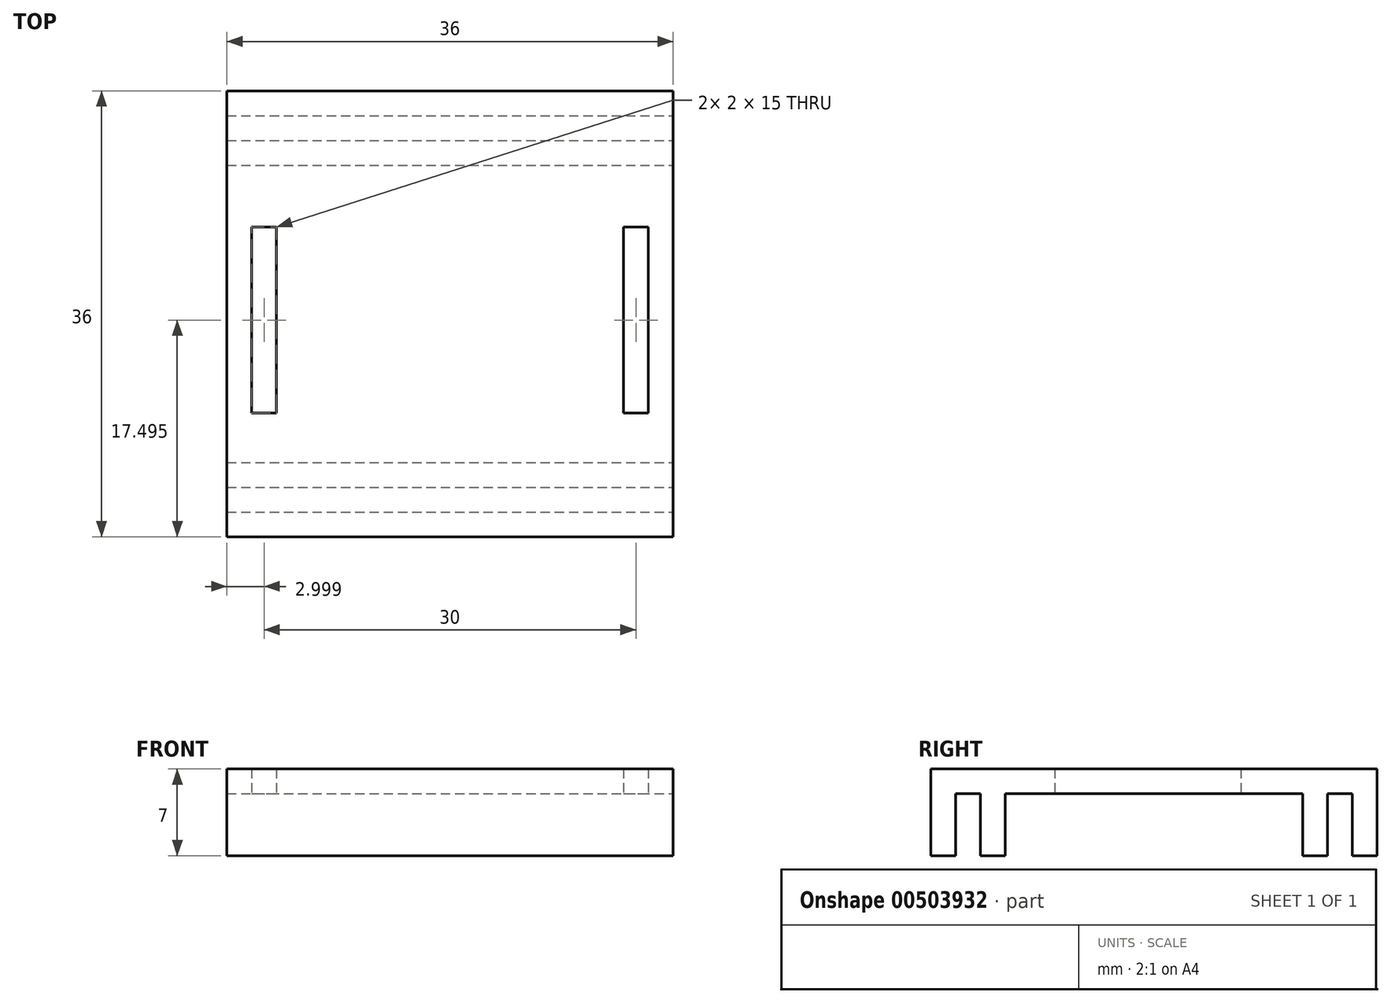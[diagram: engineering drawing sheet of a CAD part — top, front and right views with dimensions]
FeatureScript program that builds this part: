
annotation { "Feature Type Name" : "Feature", "Feature Type Description" : "" }
export const myFeature = defineFeature(function(context is Context, id is Id, definition is map)
    precondition{}
    {
        {
            var Q0;
            Q0=qCreatedBy(makeId("Top.planeOp"),FACE);
            var sketch = newSketch(context, id + "F0", { "sketchPlane" : qUnion([Q0])});
            skLineSegment(sketch, "E0.bottom", {"start": v(-16.57, 20.26) * mm, "end": v(19.43, 20.26) * mm});
            skLineSegment(sketch, "E0.top", {"start": v(-16.57, -15.74) * mm, "end": v(19.43, -15.74) * mm});
            skLineSegment(sketch, "E0.left", {"start": v(-16.57, 20.26) * mm, "end": v(-16.57, -15.74) * mm});
            skLineSegment(sketch, "E0.right", {"start": v(19.43, 20.26) * mm, "end": v(19.43, -15.74) * mm});
            skLineSegment(sketch, "E1.bottom", {"start": v(-14.57, -5.74) * mm, "end": v(-12.57, -5.74) * mm});
            skLineSegment(sketch, "E1.top", {"start": v(-14.57, 9.26) * mm, "end": v(-12.57, 9.26) * mm});
            skLineSegment(sketch, "E1.left", {"start": v(-14.57, -5.74) * mm, "end": v(-14.57, 9.26) * mm});
            skLineSegment(sketch, "E1.right", {"start": v(-12.57, -5.74) * mm, "end": v(-12.57, 9.26) * mm});
            skLineSegment(sketch, "E2.bottom", {"start": v(15.43, -5.74) * mm, "end": v(17.43, -5.74) * mm});
            skLineSegment(sketch, "E2.top", {"start": v(15.43, 9.26) * mm, "end": v(17.43, 9.26) * mm});
            skLineSegment(sketch, "E2.left", {"start": v(15.43, -5.74) * mm, "end": v(15.43, 9.26) * mm});
            skLineSegment(sketch, "E2.right", {"start": v(17.43, -5.74) * mm, "end": v(17.43, 9.26) * mm});
            skSolve(sketch);
        }
        {
            var Q0;
            Q0 = qSketchRegion(id + "F0", true);
            extrude(context, id + "F1", {"entities" : qUnion([Q0]), "depth" : 2 * mm});
        }
        {
            var Q0;
            Q0=makeQuery(id+"F1.opExtrude","CAP_FACE",FACE,{"disambiguationData":[OSD([sQuery(id+"F0.wireOp",EDGE,"E0.bottom"),sQuery(id+"F0.wireOp",EDGE,"E0.top"),sQuery(id+"F0.wireOp",EDGE,"E0.left"),sQuery(id+"F0.wireOp",EDGE,"E0.right")])],"isStart":true});
            var sketch = newSketch(context, id + "F2", { "sketchPlane" : qUnion([Q0])});
            skLineSegment(sketch, "E3.bottom", {"start": v(-16.57, 15.74) * mm, "end": v(19.43, 15.74) * mm});
            skLineSegment(sketch, "E3.top", {"start": v(-16.57, 13.74) * mm, "end": v(19.43, 13.74) * mm});
            skLineSegment(sketch, "E3.left", {"start": v(-16.57, 15.74) * mm, "end": v(-16.57, 13.74) * mm});
            skLineSegment(sketch, "E3.right", {"start": v(19.43, 15.74) * mm, "end": v(19.43, 13.74) * mm});
            skLineSegment(sketch, "E4.bottom", {"start": v(-16.57, 9.74) * mm, "end": v(19.43, 9.74) * mm});
            skLineSegment(sketch, "E4.top", {"start": v(-16.57, 11.74) * mm, "end": v(19.43, 11.74) * mm});
            skLineSegment(sketch, "E4.left", {"start": v(-16.57, 9.74) * mm, "end": v(-16.57, 11.74) * mm});
            skLineSegment(sketch, "E4.right", {"start": v(19.43, 9.74) * mm, "end": v(19.43, 11.74) * mm});
            skLineSegment(sketch, "E5.bottom", {"start": v(-16.57, -20.26) * mm, "end": v(19.43, -20.26) * mm});
            skLineSegment(sketch, "E5.top", {"start": v(-16.57, -18.26) * mm, "end": v(19.43, -18.26) * mm});
            skLineSegment(sketch, "E5.left", {"start": v(-16.57, -20.26) * mm, "end": v(-16.57, -18.26) * mm});
            skLineSegment(sketch, "E5.right", {"start": v(19.43, -20.26) * mm, "end": v(19.43, -18.26) * mm});
            skLineSegment(sketch, "E6.bottom", {"start": v(-16.57, -16.26) * mm, "end": v(19.43, -16.26) * mm});
            skLineSegment(sketch, "E6.top", {"start": v(-16.57, -14.26) * mm, "end": v(19.43, -14.26) * mm});
            skLineSegment(sketch, "E6.left", {"start": v(-16.57, -16.26) * mm, "end": v(-16.57, -14.26) * mm});
            skLineSegment(sketch, "E6.right", {"start": v(19.43, -16.26) * mm, "end": v(19.43, -14.26) * mm});
            skSolve(sketch);
        }
        {
            var Q0;
            Q0 = qSketchRegion(id + "F2", true);
            extrude(context, id + "F3", {"entities" : qUnion([Q0]), "operationType" : NewBodyOperationType.ADD, "depth" : 5 * mm});
        }
    });
